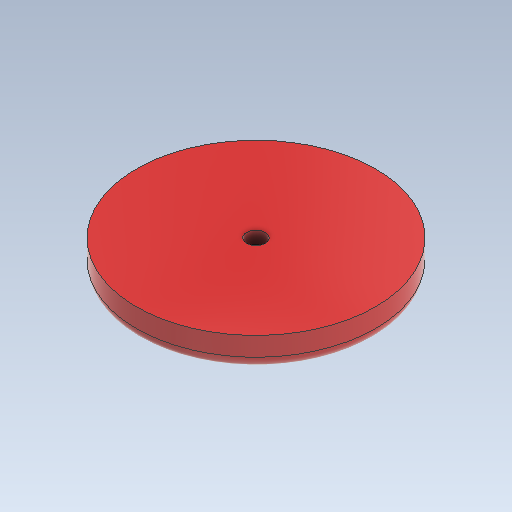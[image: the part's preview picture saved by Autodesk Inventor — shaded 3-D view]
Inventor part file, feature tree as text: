
AUTODESK INVENTOR PART (.ipt)
format: ipt  version: 2020 (Build 240168000, 168)  size: 157,184 bytes
history: native  units: mm
features: fillet x2, revolve x1, sketch x1
ambient origin geometry x8: Origin, YZ Plane, XZ Plane, XY Plane, X Axis, Y Axis, Z Axis, Center Point
bodies: Solid1 (feature_tree)
feature tree (4):
  revolve  "Revolution1"  [1 undecoded]
  fillet  "Fillet2"  Radius=5.0mm
  fillet  "Fillet3"  Radius=1.5mm
  sketch  "Sketch1"  dims[d5=19.0mm d12=2.0mm d16=5.0mm d17=1.5mm d18=90.0deg d23=2.0mm d24=90.0deg d25=4.0mm d26=0.5mm d27=2.0mm]
note: 1 required parameter value undecoded (feature->parameter linkage not recoverable at this tier; creation-order binding heuristic only, values carry confidence <= 0.55)
